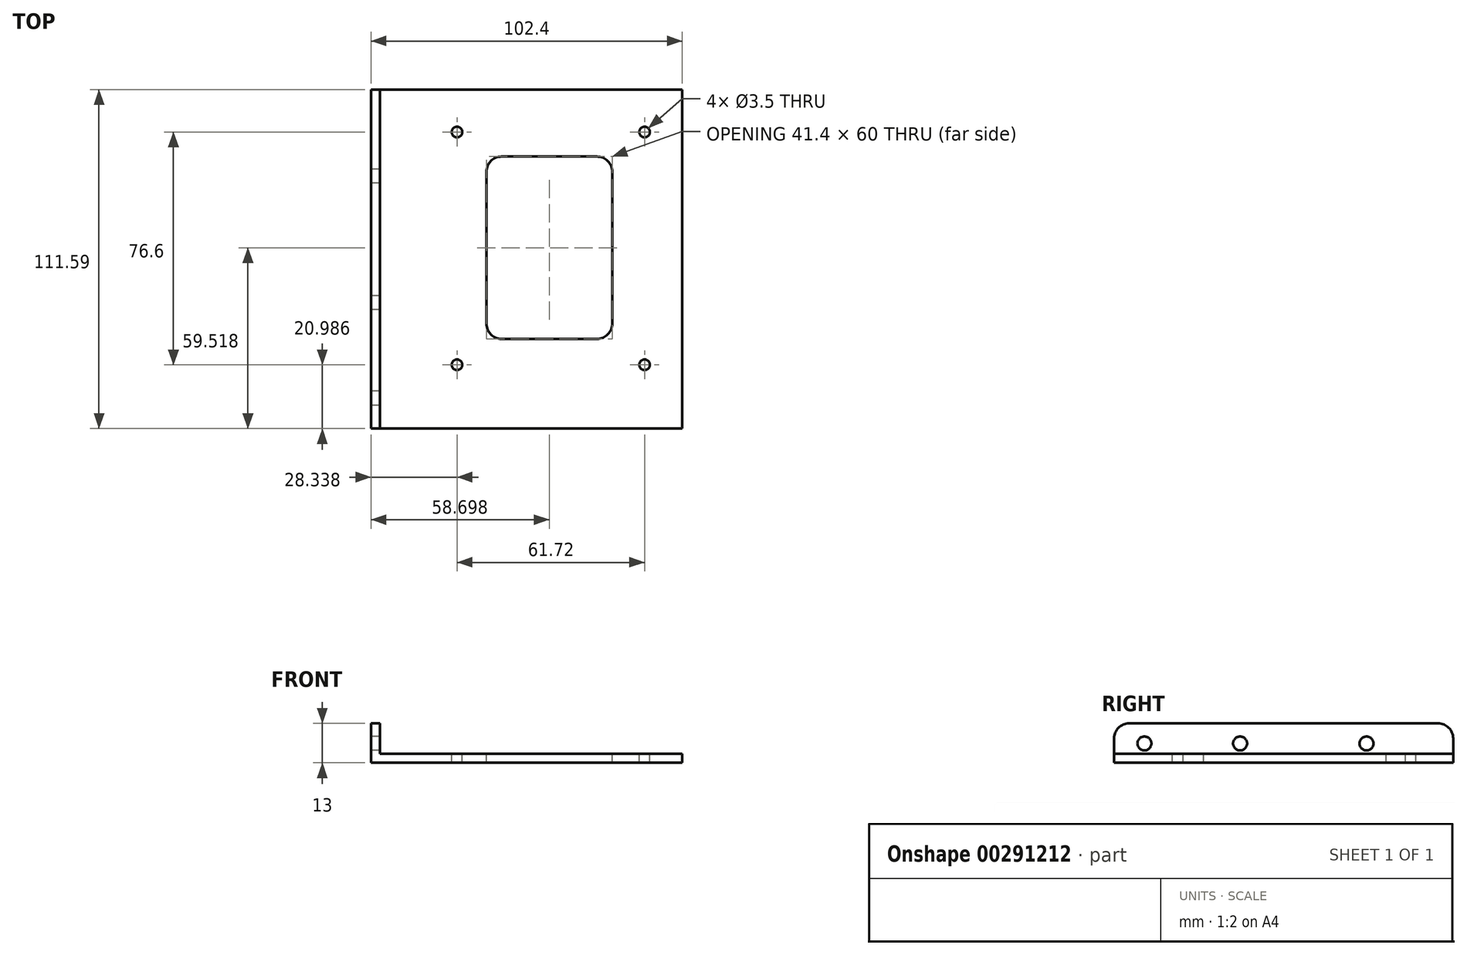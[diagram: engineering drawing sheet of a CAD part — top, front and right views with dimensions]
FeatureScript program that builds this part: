
annotation { "Feature Type Name" : "Feature", "Feature Type Description" : "" }
export const myFeature = defineFeature(function(context is Context, id is Id, definition is map)
    precondition{}
    {
        {
            var Q0;
            Q0=qCreatedBy(makeId("Top.planeOp"),FACE);
            var sketch = newSketch(context, id + "F0", { "sketchPlane" : qUnion([Q0])});
            skLineSegment(sketch, "E0.bottom", {"start": v(-63.5, 99.79) * mm, "end": v(38.9, 99.79) * mm});
            skLineSegment(sketch, "E0.top", {"start": v(-63.5, -47.21) * mm, "end": v(38.9, -47.21) * mm});
            skLineSegment(sketch, "E0.left", {"start": v(-63.5, 99.79) * mm, "end": v(-63.5, -47.21) * mm});
            skLineSegment(sketch, "E0.right", {"start": v(38.9, 99.79) * mm, "end": v(38.9, -47.21) * mm});
            skSolve(sketch);
        }
        {
            var Q0;
            Q0 = qSketchRegion(id + "F0", true);
            extrude(context, id + "F1", {"entities" : qUnion([Q0]), "depth" : 3 * mm});
        }
        {
            var Q0;
            Q0=makeQuery(id+"F1.opExtrude","CAP_FACE",FACE,{"disambiguationData":[OSD([sQuery(id+"F0.wireOp",EDGE,"E0.bottom"),sQuery(id+"F0.wireOp",EDGE,"E0.top"),sQuery(id+"F0.wireOp",EDGE,"E0.left"),sQuery(id+"F0.wireOp",EDGE,"E0.right")])],"isStart":false});
            var sketch = newSketch(context, id + "F2", { "sketchPlane" : qUnion([Q0])});
            skLineSegment(sketch, "E1.bottom", {"start": v(-63.5, -47.21) * mm, "end": v(-60.5, -47.21) * mm});
            skLineSegment(sketch, "E1.top", {"start": v(-63.5, 99.79) * mm, "end": v(-60.5, 99.79) * mm});
            skLineSegment(sketch, "E1.left", {"start": v(-63.5, -47.21) * mm, "end": v(-63.5, 99.79) * mm});
            skLineSegment(sketch, "E1.right", {"start": v(-60.5, -47.21) * mm, "end": v(-60.5, 99.79) * mm});
            skSolve(sketch);
        }
        {
            var Q0;
            Q0 = qSketchRegion(id + "F2", true);
            extrude(context, id + "F3", {"entities" : qUnion([Q0]), "operationType" : NewBodyOperationType.ADD, "depth" : 10 * mm});
        }
        {
            var Q0;
            Q0=makeQuery(id+"F1.opExtrude","SWEPT_FACE",FACE,{"disambiguationData":[OSD([sQuery(id+"F0.wireOp",EDGE,"E0.right")])]});
            var Q1;
            Q1=makeQuery(id+"F3.boolean.opBoolean","MERGE",FACE,{"derivedFrom":[makeQuery(id+"F1.opExtrude","SWEPT_FACE",FACE,{"disambiguationData":[OSD([sQuery(id+"F0.wireOp",EDGE,"E0.left")])]}),makeQuery(id+"F3.opExtrude","SWEPT_FACE",FACE,{"disambiguationData":[OSD([sQuery(id+"F2.wireOp",EDGE,"E1.left")])]})]});
            cPlane(context, id + "F4", {"entities" : qUnion([Q0, Q1]), "cplaneType" : CPlaneType.MID_PLANE, "offset" : 25 * mm, "width" : 150 * mm, "height" : 150 * mm});
        }
        {
            var Q0;
            Q0=makeQuery(id+"F3.boolean.opBoolean","MERGE",FACE,{"derivedFrom":[makeQuery(id+"F1.opExtrude","SWEPT_FACE",FACE,{"disambiguationData":[OSD([sQuery(id+"F0.wireOp",EDGE,"E0.left")])]}),makeQuery(id+"F3.opExtrude","SWEPT_FACE",FACE,{"disambiguationData":[OSD([sQuery(id+"F2.wireOp",EDGE,"E1.left")])]})]});
            var sketch = newSketch(context, id + "F5", { "sketchPlane" : qUnion([Q0])});
            skCircle(sketch, "E2", {"center": v(1.81, 6.35) * mm, "radius": 2.3 * mm});
            skCircle(sketch, "E3", {"center": v(-29.68, 6.35) * mm, "radius": 2.3 * mm});
            skCircle(sketch, "E4", {"center": v(-71.29, 6.35) * mm, "radius": 2.3 * mm});
            skSolve(sketch);
        }
        {
            var Q0;
            Q0 = qSketchRegion(id + "F5", true);
            extrude(context, id + "F6", {"entities" : qUnion([Q0]), "operationType" : NewBodyOperationType.REMOVE, "endBound" : BoundingType.THROUGH_ALL, "oppositeDirection" : true, "depth" : 25 * mm});
        }
        {
            var Q0;
            Q0=makeQuery(id+"F1.opExtrude","CAP_FACE",FACE,{"disambiguationData":[OSD([sQuery(id+"F0.wireOp",EDGE,"E0.bottom"),sQuery(id+"F0.wireOp",EDGE,"E0.top"),sQuery(id+"F0.wireOp",EDGE,"E0.left"),sQuery(id+"F0.wireOp",EDGE,"E0.right")])],"isStart":false});
            var sketch = newSketch(context, id + "F7", { "sketchPlane" : qUnion([Q0])});
            skCircle(sketch, "E5", {"center": v(18.56, 85.79) * mm, "radius": 1.75 * mm});
            skCircle(sketch, "E6", {"center": v(-43.16, 85.79) * mm, "radius": 1.75 * mm});
            skCircle(sketch, "E7", {"center": v(18.56, 9.19) * mm, "radius": 1.75 * mm});
            skCircle(sketch, "E8", {"center": v(-43.16, 9.19) * mm, "radius": 1.75 * mm});
            skCircle(sketch, "E9.1.0.0", {"center": v(26.56, 85.79) * mm, "radius": 1.75 * mm});
            skCircle(sketch, "E9.1.0.1", {"center": v(-35.16, 85.79) * mm, "radius": 1.75 * mm});
            skCircle(sketch, "E9.1.0.2", {"center": v(-35.16, 9.19) * mm, "radius": 1.75 * mm});
            skCircle(sketch, "E9.1.0.3", {"center": v(26.56, 9.19) * mm, "radius": 1.75 * mm});
            skLineSegment(sketch, "E9.direction1", {"start": v(-43.16, 9.19) * mm, "end": v(-35.16, 9.19) * mm, "construction": true});
            skSolve(sketch);
        }
        {
            var Q0;
            Q0=makeQuery(id+"F7.imprint","IMPRINT",FACE,{"disambiguationData":[TD([[makeQuery(id+"F7.imprint","IMPRINT",EDGE,{"derivedFrom":sQuery(id+"F7.wireOp",EDGE,"E9.1.0.3")}),1.0]])]});
            var Q1;
            Q1=makeQuery(id+"F7.imprint","IMPRINT",FACE,{"disambiguationData":[TD([[makeQuery(id+"F7.imprint","IMPRINT",EDGE,{"derivedFrom":sQuery(id+"F7.wireOp",EDGE,"E9.1.0.2")}),1.0]])]});
            var Q2;
            Q2=makeQuery(id+"F7.imprint","IMPRINT",FACE,{"disambiguationData":[TD([[makeQuery(id+"F7.imprint","IMPRINT",EDGE,{"derivedFrom":sQuery(id+"F7.wireOp",EDGE,"E9.1.0.1")}),1.0]])]});
            var Q3;
            Q3=makeQuery(id+"F7.imprint","IMPRINT",FACE,{"disambiguationData":[TD([[makeQuery(id+"F7.imprint","IMPRINT",EDGE,{"derivedFrom":sQuery(id+"F7.wireOp",EDGE,"E9.1.0.0")}),1.0]])]});
            extrude(context, id + "F8", {"entities" : qUnion([Q0, Q1, Q2, Q3]), "operationType" : NewBodyOperationType.REMOVE, "endBound" : BoundingType.THROUGH_ALL, "oppositeDirection" : true, "depth" : 25 * mm});
        }
        {
            var Q0;
            Q0=makeQuery(id+"F1.opExtrude","CAP_FACE",FACE,{"disambiguationData":[OSD([sQuery(id+"F0.wireOp",EDGE,"E0.bottom"),sQuery(id+"F0.wireOp",EDGE,"E0.top"),sQuery(id+"F0.wireOp",EDGE,"E0.left"),sQuery(id+"F0.wireOp",EDGE,"E0.right")])],"isStart":false});
            var sketch = newSketch(context, id + "F9", { "sketchPlane" : qUnion([Q0])});
            skLineSegment(sketch, "E10.bottom", {"start": v(15.9, 17.72) * mm, "end": v(-25.5, 17.72) * mm});
            skLineSegment(sketch, "E10.top", {"start": v(15.9, 77.72) * mm, "end": v(-25.5, 77.72) * mm});
            skLineSegment(sketch, "E10.left", {"start": v(15.9, 17.72) * mm, "end": v(15.9, 77.72) * mm});
            skLineSegment(sketch, "E10.right", {"start": v(-25.5, 17.72) * mm, "end": v(-25.5, 77.72) * mm});
            skLineSegment(sketch, "E11.bottom", {"start": v(43.89, -51.25) * mm, "end": v(-71.44, -51.25) * mm});
            skLineSegment(sketch, "E11.top", {"start": v(43.89, -11.8) * mm, "end": v(-71.44, -11.8) * mm});
            skLineSegment(sketch, "E11.left", {"start": v(43.89, -51.25) * mm, "end": v(43.89, -11.8) * mm});
            skLineSegment(sketch, "E11.right", {"start": v(-71.44, -51.25) * mm, "end": v(-71.44, -11.8) * mm});
            skSolve(sketch);
        }
        {
            var Q0;
            Q0=makeQuery(id+"F9.imprint","IMPRINT",FACE,{"disambiguationData":[TD([[makeQuery(id+"F9.imprint","IMPRINT",EDGE,{"derivedFrom":sQuery(id+"F9.wireOp",EDGE,"E10.bottom")}),-1.0]])]});
            var Q1;
            {var subQ6=makeQuery(id+"F1.opExtrude","CAP_EDGE",EDGE,{"disambiguationData":[OSD([sQuery(id+"F0.wireOp",EDGE,"E0.top")])],"isStart":false});Q1=makeQuery(id+"F9.imprint","IMPRINT",FACE,{"disambiguationData":[TD([[makeQuery(id+"F9.imprint","IMPRINT",EDGE,{"derivedFrom":subQ6}),1.0]])]});}
            var Q2;
            Q2=makeQuery(id+"F9.imprint","IMPRINT",FACE,{"disambiguationData":[TD([[makeQuery(id+"F9.imprint","IMPRINT",EDGE,{"derivedFrom":sQuery(id+"F9.wireOp",EDGE,"E11.bottom")}),-1.0]])]});
            extrude(context, id + "F10", {"entities" : qUnion([Q0, Q1, Q2]), "operationType" : NewBodyOperationType.REMOVE, "endBound" : BoundingType.SYMMETRIC, "oppositeDirection" : true, "depth" : 25 * mm});
        }
        {
            var Q0;
            Q0=makeQuery(id+"F10.boolean.opBoolean","COPY",EDGE,{"derivedFrom":makeQuery(id+"F10.opExtrude","SWEPT_EDGE",EDGE,{"disambiguationData":[OSD([sQuery(id+"F0.wireOp",EDGE,"E0.top"),sQuery(id+"F9.wireOp",EDGE,"vKdkQJEl-uckU-Jc9d-UXZr-hBO2NRbwrfet.bottom"),sQuery(id+"F9.wireOp",EDGE,"vKdkQJEl-uckU-Jc9d-UXZr-hBO2NRbwrfet.right")])]})});
            var Q1;
            Q1=makeQuery(id+"F10.boolean.opBoolean","COPY",EDGE,{"derivedFrom":makeQuery(id+"F10.opExtrude","SWEPT_EDGE",EDGE,{"disambiguationData":[OSD([sQuery(id+"F0.wireOp",EDGE,"E0.top"),sQuery(id+"F9.wireOp",EDGE,"vKdkQJEl-uckU-Jc9d-UXZr-hBO2NRbwrfet.bottom"),sQuery(id+"F9.wireOp",EDGE,"vKdkQJEl-uckU-Jc9d-UXZr-hBO2NRbwrfet.left")])]})});
            var Q2;
            Q2=makeQuery(id+"F10.boolean.opBoolean","COPY",EDGE,{"derivedFrom":makeQuery(id+"F10.opExtrude","SWEPT_EDGE",EDGE,{"disambiguationData":[OSD([sQuery(id+"F9.wireOp",EDGE,"vKdkQJEl-uckU-Jc9d-UXZr-hBO2NRbwrfet.top"),sQuery(id+"F9.wireOp",EDGE,"vKdkQJEl-uckU-Jc9d-UXZr-hBO2NRbwrfet.left")])]})});
            var Q3;
            Q3=makeQuery(id+"FGaxl9y5x9EvqOz_1.1.F3.opExtrude","CAP_EDGE",EDGE,{"disambiguationData":[OSD([sQuery(id+"F2.wireOp",EDGE,"E1.bottom")])],"isStart":false});
            var Q4;
            Q4=makeQuery(id+"F10.boolean.opBoolean","COPY",EDGE,{"derivedFrom":makeQuery(id+"F10.opExtrude","SWEPT_EDGE",EDGE,{"disambiguationData":[OSD([sQuery(id+"F9.wireOp",EDGE,"vKdkQJEl-uckU-Jc9d-UXZr-hBO2NRbwrfet.top"),sQuery(id+"F9.wireOp",EDGE,"vKdkQJEl-uckU-Jc9d-UXZr-hBO2NRbwrfet.right")])]})});
            var Q5;
            Q5=makeQuery(id+"F3.opExtrude","CAP_EDGE",EDGE,{"disambiguationData":[OSD([sQuery(id+"F2.wireOp",EDGE,"E1.bottom")])],"isStart":false});
            var Q6;
            Q6=makeQuery(id+"F3.opExtrude","CAP_EDGE",EDGE,{"disambiguationData":[OSD([sQuery(id+"F2.wireOp",EDGE,"E1.top")])],"isStart":false});
            var Q7;
            Q7=makeQuery(id+"FGaxl9y5x9EvqOz_1.1.F3.opExtrude","CAP_EDGE",EDGE,{"disambiguationData":[OSD([sQuery(id+"F2.wireOp",EDGE,"E1.top")])],"isStart":false});
            var Q8;
            Q8=makeQuery(id+"F10.boolean.opBoolean","INTERSECT",EDGE,{"derivedFrom":[makeQuery(id+"FGaxl9y5x9EvqOz_1.1.F3.opExtrude","CAP_FACE",FACE,{"disambiguationData":[OSD([sQuery(id+"F2.wireOp",EDGE,"E1.bottom"),sQuery(id+"F2.wireOp",EDGE,"E1.top"),sQuery(id+"F2.wireOp",EDGE,"E1.left"),sQuery(id+"F2.wireOp",EDGE,"E1.right")])],"isStart":false}),makeQuery(id+"F10.opExtrude","SWEPT_FACE",FACE,{"disambiguationData":[OSD([sQuery(id+"F9.wireOp",EDGE,"E11.top")])]})]});
            var Q9;
            Q9=makeQuery(id+"F10.boolean.opBoolean","INTERSECT",EDGE,{"derivedFrom":[makeQuery(id+"F3.opExtrude","CAP_FACE",FACE,{"disambiguationData":[OSD([sQuery(id+"F2.wireOp",EDGE,"E1.bottom"),sQuery(id+"F2.wireOp",EDGE,"E1.top"),sQuery(id+"F2.wireOp",EDGE,"E1.left"),sQuery(id+"F2.wireOp",EDGE,"E1.right")])],"isStart":false}),makeQuery(id+"F10.opExtrude","SWEPT_FACE",FACE,{"disambiguationData":[OSD([sQuery(id+"F9.wireOp",EDGE,"E11.top")])]})]});
            var Q10;
            Q10=makeQuery(id+"F10.boolean.opBoolean","COPY",EDGE,{"derivedFrom":makeQuery(id+"F10.opExtrude","SWEPT_EDGE",EDGE,{"disambiguationData":[OSD([sQuery(id+"F9.wireOp",EDGE,"E10.bottom"),sQuery(id+"F9.wireOp",EDGE,"E10.left")])]})});
            var Q11;
            Q11=makeQuery(id+"F10.boolean.opBoolean","COPY",EDGE,{"derivedFrom":makeQuery(id+"F10.opExtrude","SWEPT_EDGE",EDGE,{"disambiguationData":[OSD([sQuery(id+"F9.wireOp",EDGE,"E10.bottom"),sQuery(id+"F9.wireOp",EDGE,"E10.right")])]})});
            var Q12;
            Q12=makeQuery(id+"F10.boolean.opBoolean","COPY",EDGE,{"derivedFrom":makeQuery(id+"F10.opExtrude","SWEPT_EDGE",EDGE,{"disambiguationData":[OSD([sQuery(id+"F9.wireOp",EDGE,"E10.top"),sQuery(id+"F9.wireOp",EDGE,"E10.right")])]})});
            var Q13;
            Q13=makeQuery(id+"F10.boolean.opBoolean","COPY",EDGE,{"derivedFrom":makeQuery(id+"F10.opExtrude","SWEPT_EDGE",EDGE,{"disambiguationData":[OSD([sQuery(id+"F9.wireOp",EDGE,"E10.top"),sQuery(id+"F9.wireOp",EDGE,"E10.left")])]})});
            fillet(context, id + "F11", {"entities" : qUnion([Q0, Q1, Q2, Q3, Q4, Q5, Q6, Q7, Q8, Q9, Q10, Q11, Q12, Q13]), "radius" : 5 * mm, "tangentPropagation" : true, "allowEdgeOverflow" : false});
        }
    });
